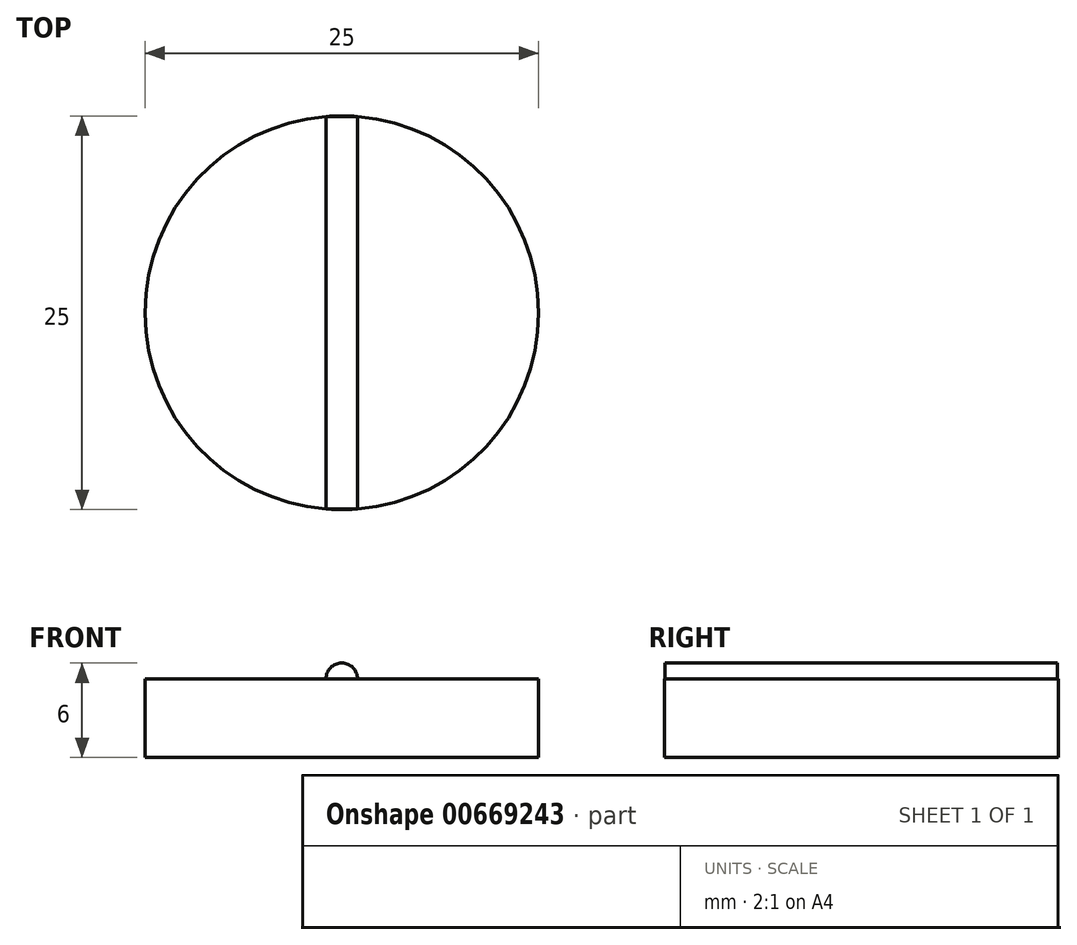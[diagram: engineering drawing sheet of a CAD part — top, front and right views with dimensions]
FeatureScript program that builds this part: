
annotation { "Feature Type Name" : "Feature", "Feature Type Description" : "" }
export const myFeature = defineFeature(function(context is Context, id is Id, definition is map)
    precondition{}
    {
        {
            var Q0;
            Q0=qCreatedBy(makeId("Top.planeOp"),FACE);
            var sketch = newSketch(context, id + "F0", { "sketchPlane" : qUnion([Q0])});
            skCircle(sketch, "E0", {"center": v(0, 0) * mm, "radius": 12.5 * mm});
            skSolve(sketch);
        }
        {
            var Q0;
            Q0=makeQuery(id+"F0.imprint","IMPRINT",FACE,{"disambiguationData":[TD([[makeQuery(id+"F0.imprint","IMPRINT",EDGE,{"derivedFrom":sQuery(id+"F0.wireOp",EDGE,"E0")}),1.0]])]});
            extrude(context, id + "F1", {"entities" : qUnion([Q0]), "depth" : 5 * mm, "offsetDistance" : 25 * mm});
        }
        {
            var Q0;
            Q0=makeQuery(id+"F1.opExtrude","CAP_FACE",FACE,{"disambiguationData":[OSD([sQuery(id+"F0.wireOp",EDGE,"E0")])],"isStart":false});
            var sketch = newSketch(context, id + "F2", { "sketchPlane" : qUnion([Q0])});
            skLineSegment(sketch, "E1.bottom", {"start": v(-1, -12.46) * mm, "end": v(1, -12.46) * mm});
            skLineSegment(sketch, "E1.top", {"start": v(-1, 12.46) * mm, "end": v(1, 12.46) * mm});
            skLineSegment(sketch, "E1.left", {"start": v(-1, -12.46) * mm, "end": v(-1, 12.46) * mm});
            skLineSegment(sketch, "E1.right", {"start": v(1, -12.46) * mm, "end": v(1, 12.46) * mm});
            skPoint(sketch, "E1.middle", {"position": v(0, 0) * mm});
            skSolve(sketch);
        }
        {
            var Q0;
            Q0=makeQuery(id+"F2.imprint","IMPRINT",FACE,{"disambiguationData":[TD([[makeQuery(id+"F2.imprint","IMPRINT",EDGE,{"derivedFrom":sQuery(id+"F2.wireOp",EDGE,"E1.bottom")}),1.0]])]});
            extrude(context, id + "F3", {"entities" : qUnion([Q0]), "operationType" : NewBodyOperationType.ADD, "depth" : 1 * mm, "offsetDistance" : 25 * mm});
        }
        {
            var Q0;
            Q0=makeQuery(id+"F3.opExtrude","CAP_EDGE",EDGE,{"disambiguationData":[OSD([sQuery(id+"F2.wireOp",EDGE,"E1.right")])],"isStart":false});
            var Q1;
            Q1=makeQuery(id+"F3.opExtrude","CAP_EDGE",EDGE,{"disambiguationData":[OSD([sQuery(id+"F2.wireOp",EDGE,"E1.left")])],"isStart":false});
            fillet(context, id + "F4", {"entities" : qUnion([Q0, Q1]), "radius" : 1 * mm, "tangentPropagation" : true, "allowEdgeOverflow" : false});
        }
    });
